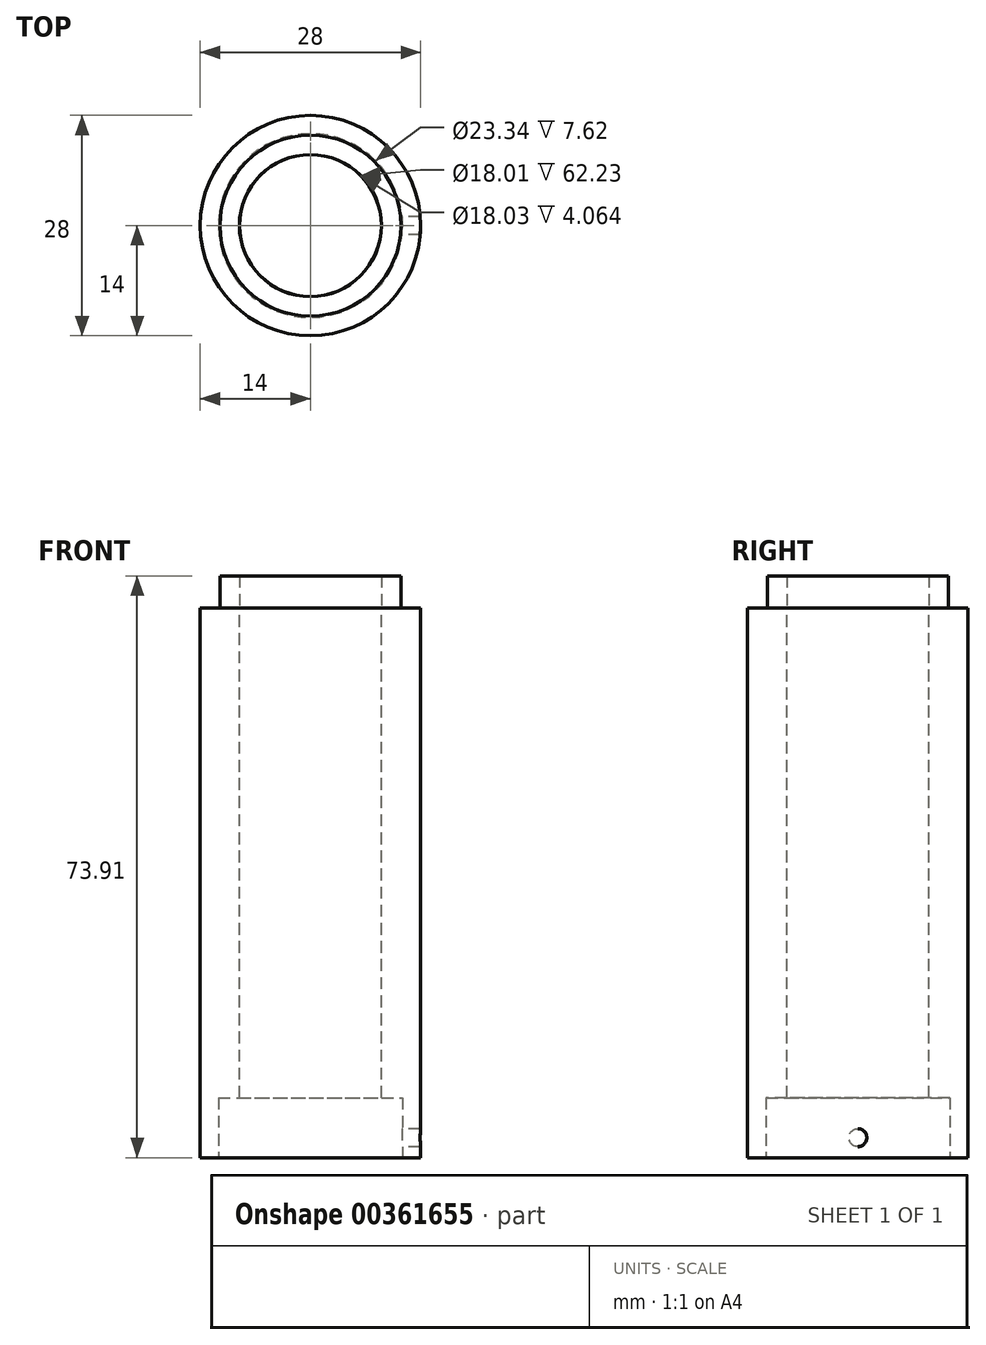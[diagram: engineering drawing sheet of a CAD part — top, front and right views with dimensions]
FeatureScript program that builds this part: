
annotation { "Feature Type Name" : "Feature", "Feature Type Description" : "" }
export const myFeature = defineFeature(function(context is Context, id is Id, definition is map)
    precondition{}
    {
        {
            var Q0;
            Q0=qCreatedBy(makeId("Top.planeOp"),FACE);
            var sketch = newSketch(context, id + "F0", { "sketchPlane" : qUnion([Q0])});
            skCircle(sketch, "E0", {"center": v(0, 0) * mm, "radius": 11.5 * mm});
            skCircle(sketch, "E1", {"center": v(0, 0) * mm, "radius": 9.02 * mm});
            skSolve(sketch);
        }
        {
            var Q0;
            Q0 = qSketchRegion(id + "F0", true);
            extrude(context, id + "F1", {"entities" : qUnion([Q0]), "depth" : 4.06 * mm});
        }
        {
            var Q0;
            Q0=makeQuery(id+"F1.opExtrude","CAP_FACE",FACE,{"disambiguationData":[OSD([sQuery(id+"F0.wireOp",EDGE,"E0"),sQuery(id+"F0.wireOp",EDGE,"E1")])],"isStart":true});
            var sketch = newSketch(context, id + "F2", { "sketchPlane" : qUnion([Q0])});
            skCircle(sketch, "E2", {"center": v(0, 0) * mm, "radius": 9 * mm});
            skCircle(sketch, "E3", {"center": v(0, 0) * mm, "radius": 14 * mm});
            skSolve(sketch);
        }
        {
            var Q0;
            Q0 = qSketchRegion(id + "F2", true);
            extrude(context, id + "F3", {"entities" : qUnion([Q0]), "operationType" : NewBodyOperationType.ADD, "depth" : 69.85 * mm});
        }
        {
            var Q0;
            Q0=makeQuery(id+"F3.opExtrude","CAP_FACE",FACE,{"disambiguationData":[OSD([sQuery(id+"F2.wireOp",EDGE,"E2"),sQuery(id+"F2.wireOp",EDGE,"E3")])],"isStart":false});
            var sketch = newSketch(context, id + "F4", { "sketchPlane" : qUnion([Q0])});
            skCircle(sketch, "E4", {"center": v(0, 0) * mm, "radius": 11.67 * mm});
            skSolve(sketch);
        }
        {
            var Q0;
            Q0 = qSketchRegion(id + "F4", true);
            extrude(context, id + "F5", {"entities" : qUnion([Q0]), "operationType" : NewBodyOperationType.REMOVE, "oppositeDirection" : true, "depth" : 7.62 * mm});
        }
        {
            var Q0;
            Q0=qCreatedBy(makeId("Right.planeOp"),FACE);
            var sketch = newSketch(context, id + "F6", { "sketchPlane" : qUnion([Q0])});
            skCircle(sketch, "E5", {"center": v(0, -67.31) * mm, "radius": 1.14 * mm});
            skSolve(sketch);
        }
        {
            var Q0;
            Q0 = qSketchRegion(id + "F6", true);
            extrude(context, id + "F7", {"entities" : qUnion([Q0]), "operationType" : NewBodyOperationType.REMOVE, "endBound" : BoundingType.THROUGH_ALL, "depth" : 50.8 * mm});
        }
    });
